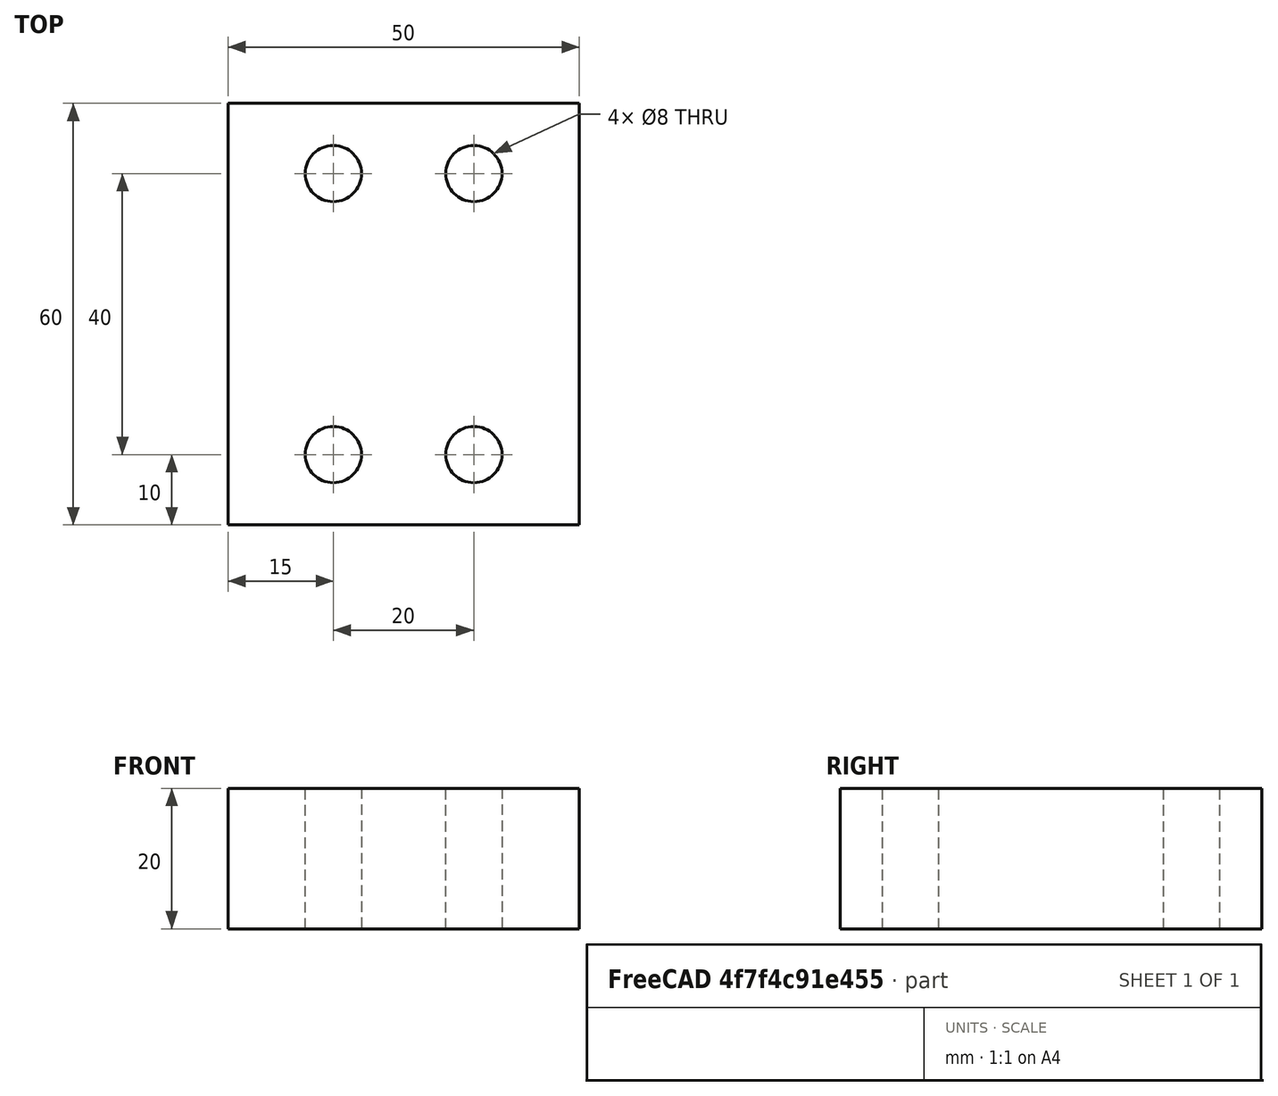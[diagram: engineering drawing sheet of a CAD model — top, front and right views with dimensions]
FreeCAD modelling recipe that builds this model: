
FCSTD DOCUMENT  (FreeCAD 0.19R17089 +1543 (Git))
Label: xrepo-003
License: All rights reserved
LicenseURL: http://en.wikipedia.org/wiki/All_rights_reserved
objects: App::FeaturePython×40, Part::FeaturePython×40, App::Link×10, App::LinkElement×8, Sketcher::SketchObject×1, PartDesign::Pad×1, PartDesign::Body×1, App::DocumentObjectGroup×1
note: 40 computed .brp shape members not serialized (recipe doc carries the construction recipe); baked Part::Feature solids carry a one-line shape summary decoded from their .brp
EXTERNAL_REF file=xrepo-lib-003.FCStd obj=Assembly
EXTERNAL_REF file=xrepo-lib-003.FCStd obj=Assembly001
EXTERNAL_REF file=xrepo-lib-003.FCStd obj=Assembly002

FEATURE [Sketcher::SketchObject] Sketch006
  MapMode = 5
  Support = -> [XY_Plane003]
  sketch-geometry (8):
    g0: Circle CenterX=-10 CenterY=20 CenterZ=0 NormalX=0 NormalY=0 NormalZ=1 AngleXU=0 Radius=4
    g1: Circle CenterX=10 CenterY=20 CenterZ=0 NormalX=0 NormalY=0 NormalZ=1 AngleXU=0 Radius=4
    g2: Circle CenterX=10 CenterY=-20 CenterZ=0 NormalX=0 NormalY=0 NormalZ=1 AngleXU=0 Radius=4
    g3: Circle CenterX=-10 CenterY=-20 CenterZ=0 NormalX=0 NormalY=0 NormalZ=1 AngleXU=0 Radius=4
    g4: LineSegment StartX=-25 StartY=30 StartZ=0 EndX=25 EndY=30 EndZ=0
    g5: LineSegment StartX=25 StartY=30 StartZ=0 EndX=25 EndY=-30 EndZ=0
    g6: LineSegment StartX=25 StartY=-30 StartZ=0 EndX=-25 EndY=-30 EndZ=0
    g7: LineSegment StartX=-25 StartY=-30 StartZ=0 EndX=-25 EndY=30 EndZ=0
  constraints (19):
    c: Equal(g0,g1)
    c: Equal(g1,g2)
    c: Equal(g2,g3)
    c: Diameter(g0) = 8  'BHD'
    c: Symmetric(g0,g1,g-2)
    c: Symmetric(g1,g2,g-1)
    c: Symmetric(g0,g3,g-1)
    c: Coincident(g4,g5)
    c: Coincident(g5,g6)
    c: Coincident(g6,g7)
    c: Coincident(g7,g4)
    c: Horizontal(g6)
    c: Vertical(g7)
    c: Symmetric(g4,g4,g-2)
    c: Symmetric(g4,g5,g-1)
    c: Distance(g3,g2) = 20  'L1'
    c: Distance(g4) = 50  'L2'
    c: Distance(g1,g2) = 40  'W1'
    c: Distance(g7) = 60  'W2'
FEATURE [PartDesign::Pad] Pad005
  ClaimChildren = false
  Length = 20
  Length2 = 100
  Profile = -> Sketch006
  Reversed = true
  Type = 0
FEATURE [PartDesign::Body] Body003
  Group = -> [Sketch006,Pad005]
  Origin = -> Origin003
  Tip = -> Pad005
FEATURE [App::FeaturePython] Constraints003  # WARN: FeaturePython — macro-defined, semantics opaque (R4)
  GroupMode = 1
  _Version = 1
FEATURE [Part::FeaturePython] Parts003  # WARN: FeaturePython — macro-defined, semantics opaque (R4)
  Group = -> [Body003]
  GroupMode = 0
FEATURE [App::Link] Link  label="Assembly000 001"
  LinkPlacement = pos=(0,0,-2) rot=(0,0,1;0rad)
  LinkedObject = -> Link007
  Placement = pos=(0,0,-2) rot=(0,0,1;0rad)
FEATURE [App::Link] Link001  label="Assembly001 001"
  LinkedObject = -> Link008
FEATURE [Part::FeaturePython] Parts004  # WARN: FeaturePython — macro-defined, semantics opaque (R4)
  Group = -> [Link,Link001]
  GroupMode = 0
FEATURE [App::Link] Link002  label="Assembly000 002"
  LinkedObject = -> Link007
FEATURE [App::Link] Link003  label="Assembly002 001"
  LinkPlacement = pos=(0,0,2) rot=(0,0,1;0rad)
  LinkedObject = -> Link009
  Placement = pos=(0,0,2) rot=(0,0,1;0rad)
FEATURE [Part::FeaturePython] Parts005  # WARN: FeaturePython — macro-defined, semantics opaque (R4)
  Group = -> [Link002,Link003]
  GroupMode = 0
FEATURE [App::Link] Link004  label="Assembly003 001"
  LinkedObject = -> Assembly003
FEATURE [App::LinkElement] Link005_i0
  LinkPlacement = pos=(-10,20,0) rot=(0,0,1;0rad)
  LinkedObject = -> Assembly005
  Placement = pos=(-10,20,0) rot=(0,0,1;0rad)
FEATURE [App::LinkElement] Link005_i1
  LinkPlacement = pos=(10,20,0) rot=(0,0,1;0rad)
  LinkedObject = -> Assembly005
  Placement = pos=(10,20,0) rot=(0,0,1;0rad)
FEATURE [App::LinkElement] Link005_i2
  LinkPlacement = pos=(10,-20,0) rot=(0,0,1;0rad)
  LinkedObject = -> Assembly005
  Placement = pos=(10,-20,0) rot=(0,0,1;0rad)
FEATURE [App::LinkElement] Link005_i3
  LinkPlacement = pos=(-10,-20,0) rot=(0,0,1;0rad)
  LinkedObject = -> Assembly005
  Placement = pos=(-10,-20,0) rot=(0,0,1;0rad)
FEATURE [App::Link] Link005  label="Assembly005 001"
  ElementCount = 4
  ElementList = -> [Link005_i0,Link005_i1,Link005_i2,Link005_i3]
  LinkedObject = -> Assembly005
FEATURE [App::LinkElement] Link006_i0
  LinkPlacement = pos=(10,20,-33) rot=(0,-1,0;0rad)
  LinkedObject = -> Assembly004
  Placement = pos=(10,20,-33) rot=(0,-1,0;0rad)
FEATURE [App::LinkElement] Link006_i1
  LinkPlacement = pos=(-10,20,-33) rot=(0,-1,0;0rad)
  LinkedObject = -> Assembly004
  Placement = pos=(-10,20,-33) rot=(0,-1,0;0rad)
FEATURE [App::LinkElement] Link006_i2
  LinkPlacement = pos=(-10,-20,-33) rot=(0,-1,0;0rad)
  LinkedObject = -> Assembly004
  Placement = pos=(-10,-20,-33) rot=(0,-1,0;0rad)
FEATURE [App::LinkElement] Link006_i3
  LinkPlacement = pos=(10,-20,-33) rot=(0,-1,0;0rad)
  LinkedObject = -> Assembly004
  Placement = pos=(10,-20,-33) rot=(0,-1,0;0rad)
FEATURE [App::Link] Link006  label="Assembly004 001"
  ElementCount = 4
  ElementList = -> [Link006_i0,Link006_i1,Link006_i2,Link006_i3]
  LinkPlacement = pos=(8.1e-13,6.55651e-06,-55) rot=(0,1,0;3.14159rad)
  LinkedObject = -> Assembly004
  Placement = pos=(8.1e-13,6.55651e-06,-55) rot=(0,1,0;3.14159rad)
FEATURE [Part::FeaturePython] Parts006  # WARN: FeaturePython — macro-defined, semantics opaque (R4)
  Group = -> [Link004,Link005,Link006]
  GroupMode = 0
FEATURE [App::Link] Link007  label="Assembly000 003"
  LinkedObject = -> <external xrepo-lib-003.FCStd>#Assembly
FEATURE [App::Link] Link008  label="Assembly001 002"
  LinkedObject = -> <external xrepo-lib-003.FCStd>#Assembly001
FEATURE [App::Link] Link009  label="Assembly002 002"
  LinkedObject = -> <external xrepo-lib-003.FCStd>#Assembly002
FEATURE [App::DocumentObjectGroup] Group  label="Repository"
  Group = -> [Link007,Link008,Link009,Assembly003,Assembly004,Assembly005]
FEATURE [Part::FeaturePython] Assembly003  label="Assembly003 000"  # WARN: FeaturePython — macro-defined, semantics opaque (R4)
  AutoRelax = true
  BuildShape = 0
  Freeze = false
  Group = -> [Constraints003,Elements003,Parts003]
  GroupMode = 1
  SolverType = 1
  Verbose = false
  _SolverType = 1
  _Version = 1
FEATURE [App::FeaturePython] Elements003  # WARN: FeaturePython — macro-defined, semantics opaque (R4)
  Group = -> [Element005,Element006,Element007,Element008,Element009,Element010,Element011,Element012,Element015]
  GroupMode = 1
FEATURE [Part::FeaturePython] Element005  # link proxy (typed FeaturePython)
  Detach = false
  LinkTransform = true
  LinkedObject = -> Body003 [Pad005.Edge23]
  _Parent = -> Elements003
FEATURE [Part::FeaturePython] Element006  # link proxy (typed FeaturePython)
  Detach = false
  LinkTransform = true
  LinkedObject = -> Body003 [Pad005.Edge20]
  _Parent = -> Elements003
FEATURE [Part::FeaturePython] Element007  # link proxy (typed FeaturePython)
  Detach = false
  LinkTransform = true
  LinkedObject = -> Body003 [Pad005.Edge17]
  _Parent = -> Elements003
FEATURE [Part::FeaturePython] Element008  # link proxy (typed FeaturePython)
  Detach = false
  LinkTransform = true
  LinkedObject = -> Body003 [Pad005.Edge14]
  _Parent = -> Elements003
FEATURE [Part::FeaturePython] Element009  # link proxy (typed FeaturePython)
  Detach = false
  LinkTransform = true
  LinkedObject = -> Body003 [Pad005.Edge24]
  _Parent = -> Elements003
FEATURE [Part::FeaturePython] Element010  # link proxy (typed FeaturePython)
  Detach = false
  LinkTransform = true
  LinkedObject = -> Body003 [Pad005.Edge21]
  _Parent = -> Elements003
FEATURE [Part::FeaturePython] Element011  # link proxy (typed FeaturePython)
  Detach = false
  LinkTransform = true
  LinkedObject = -> Body003 [Pad005.Edge18]
  _Parent = -> Elements003
FEATURE [Part::FeaturePython] Element012  # link proxy (typed FeaturePython)
  Detach = false
  LinkTransform = true
  LinkedObject = -> Body003 [Pad005.Edge15]
  _Parent = -> Elements003
FEATURE [Part::FeaturePython] Assembly004  label="Assembly004 000"  # WARN: FeaturePython — macro-defined, semantics opaque (R4)
  AutoRelax = true
  BuildShape = 0
  Freeze = false
  Group = -> [Constraints004,Elements004,Parts004]
  GroupMode = 1
  SolverType = 1
  Verbose = false
  _SolverType = 1
  _Version = 1
FEATURE [App::FeaturePython] Constraints004  # WARN: FeaturePython — macro-defined, semantics opaque (R4)
  Group = -> [Constraint]
  GroupMode = 1
  _Version = 1
FEATURE [App::FeaturePython] Elements004  # WARN: FeaturePython — macro-defined, semantics opaque (R4)
  Group = -> [_Element,_Element001,Element013]
  GroupMode = 1
FEATURE [App::FeaturePython] Constraint  label="PlaneCoincident"  # WARN: FeaturePython — macro-defined, semantics opaque (R4)
  Angle = 0
  AnglePitch = 0
  AngleRoll = 0
  Cascade = false
  ConstraintType = 2
  Disabled = false
  Group = -> [ElementLink,ElementLink001]
  GroupMode = 1
  LockAngle = false
  Multiply = false
  OffsetX = 0
  OffsetY = 0
  _ConstraintType = 35
  _Parent = -> Constraints004
FEATURE [App::FeaturePython] ElementLink  label="_Element"  # link proxy (typed FeaturePython)
  LinkTransform = true
  LinkedObject = -> _Element
  _Parent = -> Constraint
FEATURE [Part::FeaturePython] _Element  # link proxy (typed FeaturePython)
  Detach = false
  LinkTransform = true
  LinkedObject = -> Link001 [1.$Element002.]
  _Parent = -> Elements004
FEATURE [App::FeaturePython] ElementLink001  label="_Element001"  # link proxy (typed FeaturePython)
  LinkTransform = true
  LinkedObject = -> _Element001
  _Parent = -> Constraint
FEATURE [Part::FeaturePython] _Element001  # link proxy (typed FeaturePython)
  Detach = false
  LinkTransform = true
  LinkedObject = -> Link [1.$Element001.]
  _Parent = -> Elements004
FEATURE [Part::FeaturePython] Element013  # link proxy (typed FeaturePython)
  Detach = false
  LinkTransform = true
  LinkedObject = -> Link [1.$Element.]
  _Parent = -> Elements004
FEATURE [Part::FeaturePython] Assembly005  label="Assembly005 000"  # WARN: FeaturePython — macro-defined, semantics opaque (R4)
  AutoRelax = true
  BuildShape = 0
  Freeze = false
  Group = -> [Constraints005,Elements005,Parts005]
  GroupMode = 1
  SolverType = 1
  Verbose = false
  _SolverType = 1
  _Version = 1
FEATURE [App::FeaturePython] Constraints005  # WARN: FeaturePython — macro-defined, semantics opaque (R4)
  Group = -> [Constraint001]
  GroupMode = 1
  _Version = 1
FEATURE [App::FeaturePython] Elements005  # WARN: FeaturePython — macro-defined, semantics opaque (R4)
  Group = -> [_Element002,_Element003,Element014]
  GroupMode = 1
FEATURE [App::FeaturePython] Constraint001  label="PlaneCoincident001"  # WARN: FeaturePython — macro-defined, semantics opaque (R4)
  Angle = 0
  AnglePitch = 0
  AngleRoll = 0
  Cascade = false
  ConstraintType = 2
  Disabled = false
  Group = -> [ElementLink002,ElementLink003]
  GroupMode = 1
  LockAngle = false
  Multiply = false
  OffsetX = 0
  OffsetY = 0
  _ConstraintType = 35
  _Parent = -> Constraints005
FEATURE [App::FeaturePython] ElementLink002  label="_Element002"  # link proxy (typed FeaturePython)
  LinkTransform = true
  LinkedObject = -> _Element002
  _Parent = -> Constraint001
FEATURE [Part::FeaturePython] _Element002  # link proxy (typed FeaturePython)
  Detach = false
  LinkTransform = true
  LinkedObject = -> Link002 [1.$Element001.]
  _Parent = -> Elements005
FEATURE [App::FeaturePython] ElementLink003  label="_Element003"  # link proxy (typed FeaturePython)
  LinkTransform = true
  LinkedObject = -> _Element003
  _Parent = -> Constraint001
FEATURE [Part::FeaturePython] _Element003  # link proxy (typed FeaturePython)
  Detach = false
  LinkTransform = true
  LinkedObject = -> Link003 [1.$Element004.]
  _Parent = -> Elements005
FEATURE [Part::FeaturePython] Element014  # link proxy (typed FeaturePython)
  Detach = false
  LinkTransform = true
  LinkedObject = -> Link002 [1.$Element.]
  _Parent = -> Elements005
FEATURE [Part::FeaturePython] Assembly006  label="Assembly006 000"  # WARN: FeaturePython — macro-defined, semantics opaque (R4)
  AutoRelax = true
  BuildShape = 0
  Freeze = false
  Group = -> [Constraints006,Elements006,Parts006]
  GroupMode = 1
  SolverType = 1
  Verbose = false
  _SolverType = 1
  _Version = 1
FEATURE [App::FeaturePython] Constraints006  # WARN: FeaturePython — macro-defined, semantics opaque (R4)
  Group = -> [Constraint002,Constraint003,Constraint004,Constraint005,Constraint006,Constraint007,Constraint008,Constraint009,Constraint010]
  GroupMode = 1
  _Version = 1
FEATURE [App::FeaturePython] Elements006  # WARN: FeaturePython — macro-defined, semantics opaque (R4)
  Group = -> [_Element004,_Element005,_Element006,_Element007,_Element008,_Element009,_Element010,_Element011,_Element012,_Element013,_Element014,_Element015,_Element016,_Element017,_Element018,_Element019,_Element020]
  GroupMode = 1
FEATURE [App::FeaturePython] Constraint002  label="Locked"  # WARN: FeaturePython — macro-defined, semantics opaque (R4)
  ConstraintType = 0
  Disabled = false
  Group = -> [ElementLink004]
  GroupMode = 1
  _ConstraintType = 0
  _Parent = -> Constraints006
FEATURE [App::FeaturePython] ElementLink004  label="_Element004"  # link proxy (typed FeaturePython)
  LinkTransform = true
  LinkedObject = -> _Element004
  _Parent = -> Constraint002
FEATURE [Part::FeaturePython] Element015  # link proxy (typed FeaturePython)
  Detach = false
  LinkTransform = true
  LinkedObject = -> Body003 [Pad005.Face9]
  _Parent = -> Elements003
FEATURE [Part::FeaturePython] _Element004  # link proxy (typed FeaturePython)
  Detach = false
  LinkTransform = true
  LinkedObject = -> Link004 [1.$Element015.]
  _Parent = -> Elements006
FEATURE [App::FeaturePython] Constraint003  label="PlaneCoincident002"  # WARN: FeaturePython — macro-defined, semantics opaque (R4)
  Angle = 0
  AnglePitch = 0
  AngleRoll = 0
  Cascade = false
  ConstraintType = 2
  Disabled = false
  Group = -> [ElementLink005,ElementLink006]
  GroupMode = 1
  LockAngle = false
  Multiply = false
  OffsetX = 0
  OffsetY = 0
  _ConstraintType = 35
  _Parent = -> Constraints006
FEATURE [App::FeaturePython] ElementLink005  label="_Element005"  # link proxy (typed FeaturePython)
  LinkTransform = true
  LinkedObject = -> _Element005
  _Parent = -> Constraint003
FEATURE [Part::FeaturePython] _Element005  # link proxy (typed FeaturePython)
  Detach = false
  LinkTransform = true
  LinkedObject = -> Link005 [Link005_i0.1.$Element014.]
  _Parent = -> Elements006
FEATURE [App::FeaturePython] ElementLink006  label="_Element006"  # link proxy (typed FeaturePython)
  LinkTransform = true
  LinkedObject = -> _Element006
  _Parent = -> Constraint003
FEATURE [Part::FeaturePython] _Element006  # link proxy (typed FeaturePython)
  Detach = false
  LinkTransform = true
  LinkedObject = -> Link004 [1.$Element005.]
  _Parent = -> Elements006
FEATURE [App::FeaturePython] Constraint004  label="PlaneCoincident003"  # WARN: FeaturePython — macro-defined, semantics opaque (R4)
  Angle = 0
  AnglePitch = 0
  AngleRoll = 0
  Cascade = false
  ConstraintType = 2
  Disabled = false
  Group = -> [ElementLink007,ElementLink008]
  GroupMode = 1
  LockAngle = false
  Multiply = false
  OffsetX = 0
  OffsetY = 0
  _ConstraintType = 35
  _Parent = -> Constraints006
FEATURE [App::FeaturePython] ElementLink007  label="_Element007"  # link proxy (typed FeaturePython)
  LinkTransform = true
  LinkedObject = -> _Element007
  _Parent = -> Constraint004
FEATURE [Part::FeaturePython] _Element007  # link proxy (typed FeaturePython)
  Detach = false
  LinkTransform = true
  LinkedObject = -> Link004 [1.$Element006.]
  _Parent = -> Elements006
FEATURE [App::FeaturePython] ElementLink008  label="_Element008"  # link proxy (typed FeaturePython)
  LinkTransform = true
  LinkedObject = -> _Element008
  _Parent = -> Constraint004
FEATURE [Part::FeaturePython] _Element008  # link proxy (typed FeaturePython)
  Detach = false
  LinkTransform = true
  LinkedObject = -> Link005 [Link005_i1.1.$Element014.]
  _Parent = -> Elements006
FEATURE [App::FeaturePython] Constraint005  label="PlaneCoincident004"  # WARN: FeaturePython — macro-defined, semantics opaque (R4)
  Angle = 0
  AnglePitch = 0
  AngleRoll = 0
  Cascade = false
  ConstraintType = 2
  Disabled = false
  Group = -> [ElementLink009,ElementLink010]
  GroupMode = 1
  LockAngle = false
  Multiply = false
  OffsetX = 0
  OffsetY = 0
  _ConstraintType = 35
  _Parent = -> Constraints006
FEATURE [App::FeaturePython] ElementLink009  label="_Element009"  # link proxy (typed FeaturePython)
  LinkTransform = true
  LinkedObject = -> _Element009
  _Parent = -> Constraint005
FEATURE [Part::FeaturePython] _Element009  # link proxy (typed FeaturePython)
  Detach = false
  LinkTransform = true
  LinkedObject = -> Link004 [1.$Element007.]
  _Parent = -> Elements006
FEATURE [App::FeaturePython] ElementLink010  label="_Element010"  # link proxy (typed FeaturePython)
  LinkTransform = true
  LinkedObject = -> _Element010
  _Parent = -> Constraint005
FEATURE [Part::FeaturePython] _Element010  # link proxy (typed FeaturePython)
  Detach = false
  LinkTransform = true
  LinkedObject = -> Link005 [Link005_i2.1.$Element014.]
  _Parent = -> Elements006
FEATURE [App::FeaturePython] Constraint006  label="PlaneCoincident005"  # WARN: FeaturePython — macro-defined, semantics opaque (R4)
  Angle = 0
  AnglePitch = 0
  AngleRoll = 0
  Cascade = false
  ConstraintType = 2
  Disabled = false
  Group = -> [ElementLink011,ElementLink012]
  GroupMode = 1
  LockAngle = false
  Multiply = false
  OffsetX = 0
  OffsetY = 0
  _ConstraintType = 35
  _Parent = -> Constraints006
FEATURE [App::FeaturePython] ElementLink011  label="_Element011"  # link proxy (typed FeaturePython)
  LinkTransform = true
  LinkedObject = -> _Element011
  _Parent = -> Constraint006
FEATURE [Part::FeaturePython] _Element011  # link proxy (typed FeaturePython)
  Detach = false
  LinkTransform = true
  LinkedObject = -> Link004 [1.$Element008.]
  _Parent = -> Elements006
FEATURE [App::FeaturePython] ElementLink012  label="_Element012"  # link proxy (typed FeaturePython)
  LinkTransform = true
  LinkedObject = -> _Element012
  _Parent = -> Constraint006
FEATURE [Part::FeaturePython] _Element012  # link proxy (typed FeaturePython)
  Detach = false
  LinkTransform = true
  LinkedObject = -> Link005 [Link005_i3.1.$Element014.]
  _Parent = -> Elements006
FEATURE [App::FeaturePython] Constraint007  label="PlaneCoincident006"  # WARN: FeaturePython — macro-defined, semantics opaque (R4)
  Angle = 0
  AnglePitch = 0
  AngleRoll = 0
  Cascade = false
  ConstraintType = 2
  Disabled = false
  Group = -> [ElementLink013,ElementLink014]
  GroupMode = 1
  LockAngle = false
  Multiply = false
  OffsetX = 0
  OffsetY = 0
  _ConstraintType = 35
  _Parent = -> Constraints006
FEATURE [App::FeaturePython] ElementLink013  label="_Element013"  # link proxy (typed FeaturePython)
  LinkTransform = true
  LinkedObject = -> _Element013
  _Parent = -> Constraint007
FEATURE [Part::FeaturePython] _Element013  # link proxy (typed FeaturePython)
  Detach = false
  LinkTransform = true
  LinkedObject = -> Link004 [1.$Element009.]
  _Parent = -> Elements006
FEATURE [App::FeaturePython] ElementLink014  label="_Element014"  # link proxy (typed FeaturePython)
  LinkTransform = true
  LinkedObject = -> _Element014
  _Parent = -> Constraint007
FEATURE [Part::FeaturePython] _Element014  # link proxy (typed FeaturePython)
  Detach = false
  LinkTransform = true
  LinkedObject = -> Link006 [Link006_i0.1.$Element013.]
  _Parent = -> Elements006
FEATURE [App::FeaturePython] Constraint008  label="PlaneCoincident007"  # WARN: FeaturePython — macro-defined, semantics opaque (R4)
  Angle = 0
  AnglePitch = 0
  AngleRoll = 0
  Cascade = false
  ConstraintType = 2
  Disabled = false
  Group = -> [ElementLink015,ElementLink016]
  GroupMode = 1
  LockAngle = false
  Multiply = false
  OffsetX = 0
  OffsetY = 0
  _ConstraintType = 35
  _Parent = -> Constraints006
FEATURE [App::FeaturePython] ElementLink015  label="_Element015"  # link proxy (typed FeaturePython)
  LinkTransform = true
  LinkedObject = -> _Element015
  _Parent = -> Constraint008
FEATURE [Part::FeaturePython] _Element015  # link proxy (typed FeaturePython)
  Detach = false
  LinkTransform = true
  LinkedObject = -> Link004 [1.$Element010.]
  _Parent = -> Elements006
FEATURE [App::FeaturePython] ElementLink016  label="_Element016"  # link proxy (typed FeaturePython)
  LinkTransform = true
  LinkedObject = -> _Element016
  _Parent = -> Constraint008
FEATURE [Part::FeaturePython] _Element016  # link proxy (typed FeaturePython)
  Detach = false
  LinkTransform = true
  LinkedObject = -> Link006 [Link006_i1.1.$Element013.]
  _Parent = -> Elements006
FEATURE [App::FeaturePython] Constraint009  label="PlaneCoincident008"  # WARN: FeaturePython — macro-defined, semantics opaque (R4)
  Angle = 0
  AnglePitch = 0
  AngleRoll = 0
  Cascade = false
  ConstraintType = 2
  Disabled = false
  Group = -> [ElementLink017,ElementLink018]
  GroupMode = 1
  LockAngle = false
  Multiply = false
  OffsetX = 0
  OffsetY = 0
  _ConstraintType = 35
  _Parent = -> Constraints006
FEATURE [App::FeaturePython] ElementLink017  label="_Element017"  # link proxy (typed FeaturePython)
  LinkTransform = true
  LinkedObject = -> _Element017
  _Parent = -> Constraint009
FEATURE [Part::FeaturePython] _Element017  # link proxy (typed FeaturePython)
  Detach = false
  LinkTransform = true
  LinkedObject = -> Link004 [1.$Element011.]
  _Parent = -> Elements006
FEATURE [App::FeaturePython] ElementLink018  label="_Element018"  # link proxy (typed FeaturePython)
  LinkTransform = true
  LinkedObject = -> _Element018
  _Parent = -> Constraint009
FEATURE [Part::FeaturePython] _Element018  # link proxy (typed FeaturePython)
  Detach = false
  LinkTransform = true
  LinkedObject = -> Link006 [Link006_i2.1.$Element013.]
  _Parent = -> Elements006
FEATURE [App::FeaturePython] Constraint010  label="PlaneCoincident009"  # WARN: FeaturePython — macro-defined, semantics opaque (R4)
  Angle = 0
  AnglePitch = 0
  AngleRoll = 0
  Cascade = false
  ConstraintType = 2
  Disabled = false
  Group = -> [ElementLink019,ElementLink020]
  GroupMode = 1
  LockAngle = false
  Multiply = false
  OffsetX = 0
  OffsetY = 0
  _ConstraintType = 35
  _Parent = -> Constraints006
FEATURE [App::FeaturePython] ElementLink019  label="_Element019"  # link proxy (typed FeaturePython)
  LinkTransform = true
  LinkedObject = -> _Element019
  _Parent = -> Constraint010
FEATURE [Part::FeaturePython] _Element019  # link proxy (typed FeaturePython)
  Detach = false
  LinkTransform = true
  LinkedObject = -> Link004 [1.$Element012.]
  _Parent = -> Elements006
FEATURE [App::FeaturePython] ElementLink020  label="_Element020"  # link proxy (typed FeaturePython)
  LinkTransform = true
  LinkedObject = -> _Element020
  _Parent = -> Constraint010
FEATURE [Part::FeaturePython] _Element020  # link proxy (typed FeaturePython)
  Detach = false
  LinkTransform = true
  LinkedObject = -> Link006 [Link006_i3.1.$Element013.]
  _Parent = -> Elements006

RESOLVED EXTERNAL PARTS (link-assembly join: the EXTERNAL_REF files above that resolve inside this repo's crawl, each included once):
---- part xrepo-lib-003.FCStd = doc fcstd_cd6cd5374638 ----
FCSTD DOCUMENT  (FreeCAD 0.19R17089 +1543 (Git))
Label: xrepo-lib-003
License: All rights reserved
LicenseURL: http://en.wikipedia.org/wiki/All_rights_reserved
objects: Part::FeaturePython×14, Sketcher::SketchObject×9, App::FeaturePython×8, PartDesign::Pad×8, PartDesign::Body×4, PartDesign::Chamfer×2, PartDesign::Pocket×1
note: 43 computed .brp shape members not serialized (recipe doc carries the construction recipe); baked Part::Feature solids carry a one-line shape summary decoded from their .brp

FEATURE [App::FeaturePython] Constraints  # WARN: FeaturePython — macro-defined, semantics opaque (R4)
  GroupMode = 1
  _Version = 1
FEATURE [Sketcher::SketchObject] Sketch
  MapMode = 5
  Support = -> [XY_Plane]
  sketch-geometry (2):
    g0: Circle CenterX=0 CenterY=0 CenterZ=0 NormalX=0 NormalY=0 NormalZ=1 AngleXU=0 Radius=4.15
    g1: Circle CenterX=0 CenterY=0 CenterZ=0 NormalX=0 NormalY=0 NormalZ=1 AngleXU=0 Radius=8
  constraints (4):
    c: Coincident(g0,g-1)
    c: Coincident(g1,g0)
    c: Diameter(g0) = 8.3  'D1'
    c: Diameter(g1) = 16  'D2'
FEATURE [PartDesign::Pad] Pad
  ClaimChildren = false
  Length = 2
  Length2 = 100
  Profile = -> Sketch
  Type = 0
FEATURE [PartDesign::Body] Body
  Group = -> [Sketch,Pad]
  Origin = -> Origin
  Tip = -> Pad
FEATURE [Part::FeaturePython] Parts  # WARN: FeaturePython — macro-defined, semantics opaque (R4)
  Group = -> [Body]
  GroupMode = 0
FEATURE [App::FeaturePython] Constraints001  # WARN: FeaturePython — macro-defined, semantics opaque (R4)
  GroupMode = 1
  _Version = 1
FEATURE [Sketcher::SketchObject] Sketch001
  MapMode = 5
  Support = -> [XY_Plane001]
  sketch-geometry (8):
    g0: Circle CenterX=0 CenterY=0 CenterZ=0 NormalX=0 NormalY=0 NormalZ=1 AngleXU=0 Radius=4
    g1: LineSegment StartX=7.50496 StartY=0.0945881 StartZ=0 EndX=3.67056 EndY=6.54678 EndZ=0
    g2: LineSegment StartX=3.67056 StartY=6.54678 StartZ=0 EndX=-3.83439 EndY=6.45219 EndZ=0
    g3: LineSegment StartX=-3.83439 StartY=6.45219 StartZ=0 EndX=-7.50496 EndY=-0.0945881 EndZ=0
    g4: LineSegment StartX=-7.50496 StartY=-0.0945881 StartZ=0 EndX=-3.67056 EndY=-6.54678 EndZ=0
    g5: LineSegment StartX=-3.67056 StartY=-6.54678 StartZ=0 EndX=3.83439 EndY=-6.45219 EndZ=0
    g6: LineSegment StartX=3.83439 StartY=-6.45219 StartZ=0 EndX=7.50496 EndY=0.0945881 EndZ=0
    g7: Circle [constr] CenterX=0 CenterY=0 CenterZ=0 NormalX=0 NormalY=0 NormalZ=1 AngleXU=0 Radius=7.50555
  constraints (17):
    c: Coincident(g0,g-1)
    c: Diameter(g0) = 8  'D1'
    c: Coincident(g1,g2)
    c: Coincident(g2,g3)
    c: Coincident(g3,g4)
    c: Coincident(g4,g5)
    c: Coincident(g5,g6)
    c: Coincident(g6,g1)
    c: Equal(g1, g2-g6) x5
    c: PointOnObject(g1,g7)
    c: PointOnObject(g2,g7)
    c: PointOnObject(g3,g7)
    c: PointOnObject(g4,g7)
    c: PointOnObject(g5,g7)
    c: PointOnObject(g6,g7)
    c: Coincident(g7,g0)
    c: Distance(g1,g5) = 13  'WS'
FEATURE [PartDesign::Pad] Pad001
  ClaimChildren = false
  Length = 6.4
  Length2 = 100
  Profile = -> Sketch001
  Type = 0
FEATURE [PartDesign::Body] Body001
  Group = -> [Sketch001,Pad001]
  Origin = -> Origin001
  Tip = -> Pad001
FEATURE [Part::FeaturePython] Parts001  # WARN: FeaturePython — macro-defined, semantics opaque (R4)
  Group = -> [Body001]
  GroupMode = 0
FEATURE [App::FeaturePython] Constraints002  # WARN: FeaturePython — macro-defined, semantics opaque (R4)
  GroupMode = 1
  _Version = 1
FEATURE [Sketcher::SketchObject] Sketch004
  MapMode = 5
  Support = -> [XY_Plane002]
  sketch-geometry (1):
    g0: Circle CenterX=0 CenterY=0 CenterZ=0 NormalX=0 NormalY=0 NormalZ=1 AngleXU=0 Radius=6.5
  constraints (2):
    c: Coincident(g0,g-1)
    c: Diameter(g0) = 13  'DH'
FEATURE [Sketcher::SketchObject] Sketch002
  MapMode = 5
  Support = -> [XY_Plane002]
  sketch-geometry (1):
    g0: Circle CenterX=0 CenterY=0 CenterZ=0 NormalX=0 NormalY=0 NormalZ=1 AngleXU=0 Radius=4
  constraints (2):
    c: Coincident(g0,g-1)
    c: Diameter(g0) = 8  'D1'
FEATURE [PartDesign::Pad] Pad002
  ClaimChildren = false
  Length = 5
  Length2 = 100
  Profile = -> Sketch002
  Reversed = true
  Type = 0
FEATURE [Sketcher::SketchObject] Sketch003
  ExternalGeometry = -> [Pad002]
  MapMode = 5
  Placement = pos=(0,0,-5) rot=(1,0,0;3.14159rad)
  Support = -> [Pad002]
FEATURE [PartDesign::Pad] Pad003
  BaseFeature = -> Pad002
  ClaimChildren = false
  Length = 30
  Length2 = 100
  Profile = -> Sketch003
  Type = 0
FEATURE [PartDesign::Pad] Pad004
  BaseFeature = -> Pad003
  ClaimChildren = false
  Length = 6
  Length2 = 100
  Profile = -> Sketch004
  Type = 0
FEATURE [Sketcher::SketchObject] Sketch005
  MapMode = 5
  Placement = pos=(0,0,6) rot=(0,0,1;0rad)
  Support = -> [Pad004]
  sketch-geometry (7):
    g0: LineSegment StartX=3.4641 StartY=0 StartZ=0 EndX=1.73205 EndY=3 EndZ=0
    g1: LineSegment StartX=1.73205 StartY=3 StartZ=0 EndX=-1.73205 EndY=3 EndZ=0
    g2: LineSegment StartX=-1.73205 StartY=3 StartZ=0 EndX=-3.4641 EndY=0 EndZ=0
    g3: LineSegment StartX=-3.4641 StartY=0 StartZ=0 EndX=-1.73205 EndY=-3 EndZ=0
    g4: LineSegment StartX=-1.73205 StartY=-3 StartZ=0 EndX=1.73205 EndY=-3 EndZ=0
    g5: LineSegment StartX=1.73205 StartY=-3 StartZ=0 EndX=3.4641 EndY=0 EndZ=0
    g6: Circle [constr] CenterX=0 CenterY=0 CenterZ=0 NormalX=0 NormalY=0 NormalZ=1 AngleXU=0 Radius=3.4641
  constraints (16):
    c: Coincident(g0,g1)
    c: Coincident(g1,g2)
    c: Coincident(g2,g3)
    c: Coincident(g3,g4)
    c: Coincident(g4,g5)
    c: Coincident(g5,g0)
    c: Equal(g0, g1-g5) x5
    c: PointOnObject(g0,g6)
    c: PointOnObject(g1,g6)
    c: PointOnObject(g2,g6)
    c: PointOnObject(g3,g6)
    c: PointOnObject(g4,g6)
    c: PointOnObject(g5,g6)
    c: Coincident(g6,g-1)
    c: PointOnObject(g5,g-1)
    c: Distance(g0,g4) = 6  'WS'
FEATURE [PartDesign::Pocket] Pocket
  BaseFeature = -> Pad004
  ClaimChildren = false
  Length = 5
  Length2 = 100
  Profile = -> Sketch005
  Type = 0
FEATURE [PartDesign::Chamfer] Chamfer
  Base = -> Pocket [Edge6]
  BaseFeature = -> Pocket
  Size = 1.2
FEATURE [PartDesign::Body] Body002
  Group = -> [Sketch002,Pad002,Sketch003,Pad003,Sketch004,Pad004,Sketch005,Pocket,Chamfer]
  Origin = -> Origin002
  Tip = -> Chamfer
FEATURE [Part::FeaturePython] Parts002  # WARN: FeaturePython — macro-defined, semantics opaque (R4)
  Group = -> [Body002]
  GroupMode = 0
FEATURE [App::FeaturePython] Constraints003  # WARN: FeaturePython — macro-defined, semantics opaque (R4)
  GroupMode = 1
  _Version = 1
FEATURE [Sketcher::SketchObject] Sketch006
  MapMode = 5
  Support = -> [XY_Plane003]
  sketch-geometry (1):
    g0: Circle CenterX=0 CenterY=0 CenterZ=0 NormalX=0 NormalY=0 NormalZ=1 AngleXU=0 Radius=4
  constraints (2):
    c: Coincident(g0,g-1)
    c: Diameter(g0) = 8  'D1'
FEATURE [PartDesign::Pad] Pad005
  ClaimChildren = false
  Length = 5
  Length2 = 100
  Profile = -> Sketch006
  Reversed = true
  Type = 0
FEATURE [Sketcher::SketchObject] Sketch007
  ExternalGeometry = -> [Pad005]
  MapMode = 5
  Placement = pos=(0,0,-5) rot=(1,0,0;3.14159rad)
  Support = -> [Pad005]
FEATURE [PartDesign::Pad] Pad006
  BaseFeature = -> Pad005
  ClaimChildren = false
  Length = 30
  Length2 = 100
  Profile = -> Sketch007
  Type = 0
FEATURE [PartDesign::Chamfer] Chamfer001
  Base = -> Pad006 [Edge5]
  BaseFeature = -> Pad006
  Size = 1.2
FEATURE [Sketcher::SketchObject] Sketch008
  MapMode = 5
  Support = -> [XY_Plane003]
  sketch-geometry (7):
    g0: LineSegment StartX=7.50555 StartY=0 StartZ=0 EndX=3.75278 EndY=6.5 EndZ=0
    g1: LineSegment StartX=3.75278 StartY=6.5 StartZ=0 EndX=-3.75278 EndY=6.5 EndZ=0
    g2: LineSegment StartX=-3.75278 StartY=6.5 StartZ=0 EndX=-7.50555 EndY=3.3924e-11 EndZ=0
    g3: LineSegment StartX=-7.50555 StartY=3.3924e-11 StartZ=0 EndX=-3.75278 EndY=-6.5 EndZ=0
    g4: LineSegment StartX=-3.75278 StartY=-6.5 StartZ=0 EndX=3.75278 EndY=-6.5 EndZ=0
    g5: LineSegment StartX=3.75278 StartY=-6.5 StartZ=0 EndX=7.50555 EndY=0 EndZ=0
    g6: Circle [constr] CenterX=0 CenterY=0 CenterZ=0 NormalX=0 NormalY=0 NormalZ=1 AngleXU=0 Radius=7.50555
  constraints (16):
    c: Coincident(g0,g1)
    c: Coincident(g1,g2)
    c: Coincident(g2,g3)
    c: Coincident(g3,g4)
    c: Coincident(g4,g5)
    c: Coincident(g5,g0)
    c: Equal(g0, g1-g5) x5
    c: PointOnObject(g0,g6)
    c: PointOnObject(g1,g6)
    c: PointOnObject(g2,g6)
    c: PointOnObject(g3,g6)
    c: PointOnObject(g4,g6)
    c: PointOnObject(g5,g6)
    c: Coincident(g6,g-1)
    c: PointOnObject(g5,g-1)
    c: Distance(g0,g4) = 13  'WS'
FEATURE [PartDesign::Pad] Pad007
  BaseFeature = -> Chamfer001
  ClaimChildren = false
  Length = 6.4
  Length2 = 100
  Profile = -> Sketch008
  Type = 0
FEATURE [PartDesign::Body] Body003
  Group = -> [Sketch006,Pad005,Sketch007,Pad006,Chamfer001,Sketch008,Pad007]
  Origin = -> Origin003
  Tip = -> Pad007
FEATURE [Part::FeaturePython] Parts003  # WARN: FeaturePython — macro-defined, semantics opaque (R4)
  Group = -> [Body003]
  GroupMode = 0
FEATURE [Part::FeaturePython] Element  # link proxy (typed FeaturePython)
  Detach = false
  LinkTransform = true
  LinkedObject = -> Body [Pad.Edge5]
  _Parent = -> Elements
FEATURE [Part::FeaturePython] Element001  # link proxy (typed FeaturePython)
  Detach = false
  LinkTransform = true
  LinkedObject = -> Body [Pad.Edge6]
  _Parent = -> Elements
FEATURE [App::FeaturePython] Elements  # WARN: FeaturePython — macro-defined, semantics opaque (R4)
  Group = -> [Element,Element001]
  GroupMode = 1
FEATURE [Part::FeaturePython] Assembly  label="Assembly000 000"  # WARN: FeaturePython — macro-defined, semantics opaque (R4)
  AutoRelax = true
  BuildShape = 0
  Freeze = false
  Group = -> [Constraints,Elements,Parts]
  GroupMode = 1
  SolverType = 1
  Verbose = false
  _SolverType = 1
  _Version = 1
FEATURE [Part::FeaturePython] Element002  # link proxy (typed FeaturePython)
  Detach = false
  LinkTransform = true
  LinkedObject = -> Body001 [Pad001.Edge20]
  _Parent = -> Elements001
FEATURE [Part::FeaturePython] Element003  # link proxy (typed FeaturePython)
  Detach = false
  LinkTransform = true
  LinkedObject = -> Body001 [Pad001.Edge21]
  _Parent = -> Elements001
FEATURE [App::FeaturePython] Elements001  # WARN: FeaturePython — macro-defined, semantics opaque (R4)
  Group = -> [Element002,Element003]
  GroupMode = 1
FEATURE [Part::FeaturePython] Assembly001  label="Assembly001 000"  # WARN: FeaturePython — macro-defined, semantics opaque (R4)
  AutoRelax = true
  BuildShape = 0
  Freeze = false
  Group = -> [Constraints001,Elements001,Parts001]
  GroupMode = 1
  SolverType = 1
  Verbose = false
  _SolverType = 1
  _Version = 1
FEATURE [Part::FeaturePython] Element004  # link proxy (typed FeaturePython)
  Detach = false
  LinkTransform = true
  LinkedObject = -> Body002 [Pad002.Edge2]
  _Parent = -> Elements002
FEATURE [App::FeaturePython] Elements002  # WARN: FeaturePython — macro-defined, semantics opaque (R4)
  Group = -> [Element004]
  GroupMode = 1
FEATURE [Part::FeaturePython] Assembly002  label="Assembly002 000"  # WARN: FeaturePython — macro-defined, semantics opaque (R4)
  AutoRelax = true
  BuildShape = 0
  Freeze = false
  Group = -> [Constraints002,Elements002,Parts002]
  GroupMode = 1
  SolverType = 1
  Verbose = false
  _SolverType = 1
  _Version = 1
FEATURE [Part::FeaturePython] Assembly003  label="Assembly003 000"  # WARN: FeaturePython — macro-defined, semantics opaque (R4)
  AutoRelax = true
  BuildShape = 0
  Freeze = false
  Group = -> [Constraints003,Elements003,Parts003]
  GroupMode = 1
  SolverType = 1
  Verbose = false
  _SolverType = 1
  _Version = 1
FEATURE [App::FeaturePython] Elements003  # WARN: FeaturePython — macro-defined, semantics opaque (R4)
  Group = -> [Element005]
  GroupMode = 1
FEATURE [Part::FeaturePython] Element005  label="Element004"  # link proxy (typed FeaturePython)
  Detach = false
  LinkTransform = true
  LinkedObject = -> Body003 [Pad007.Edge7]
  _Parent = -> Elements003
